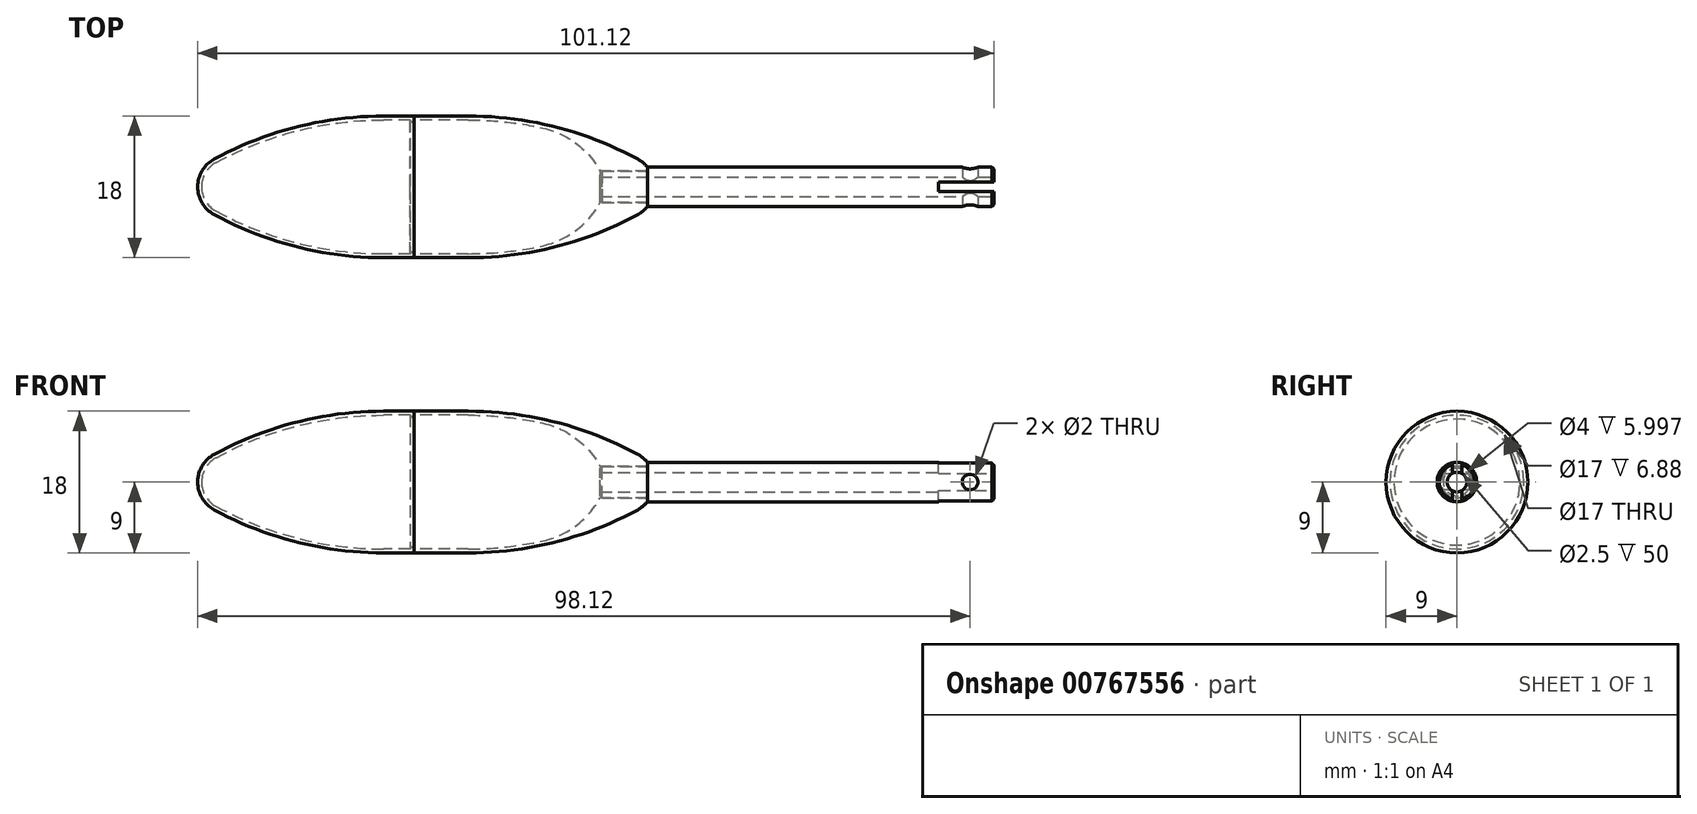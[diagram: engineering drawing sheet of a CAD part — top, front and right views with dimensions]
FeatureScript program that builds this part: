
annotation { "Feature Type Name" : "Feature", "Feature Type Description" : "" }
export const myFeature = defineFeature(function(context is Context, id is Id, definition is map)
    precondition{}
    {
        {
            var Q0;
            Q0=qCreatedBy(makeId("Front.planeOp"),FACE);
            var sketch = newSketch(context, id + "F0", { "sketchPlane" : qUnion([Q0])});
            skLineSegment(sketch, "E0", {"start": v(0, 0) * mm, "end": v(0, 8.5) * mm});
            skLineSegment(sketch, "E1", {"start": v(0, 8.5) * mm, "end": v(-3, 8.5) * mm});
            skLineSegment(sketch, "E2", {"start": v(-3, 8.5) * mm, "end": v(-3, 9) * mm});
            skLineSegment(sketch, "E3", {"start": v(-3, 9) * mm, "end": v(-6.88, 9) * mm});
            skArc(sketch, "E4", {"start": v(-6.88, 9) * mm, "mid": v(-18, 7.6) * mm, "end": v(-28.41, 3.51) * mm});
            skArc(sketch, "E5", {"start": v(-28.41, 3.51) * mm, "mid": v(-29.94, 2.04) * mm, "end": v(-30.5, 0) * mm});
            skLineSegment(sketch, "E6", {"start": v(-30.5, 0) * mm, "end": v(0, 0) * mm});
            skSolve(sketch);
        }
        {
            var Q0;
            Q0 = qSketchRegion(id + "F0", true);
            var Q1;
            Q1=sQuery(id+"F0.wireOp",EDGE,"E6");
            revolve(context, id + "F1", {"surfaceOperationType" : NewSurfaceOperationType.NEW, "entities" : qUnion([Q0]), "axis" : qUnion([Q1]), "revolveType" : RevolveType.FULL});
        }
        {
            var Q0;
            Q0=makeQuery(id+"F1.opRevolve","SWEPT_FACE",FACE,{"disambiguationData":[OSD([sQuery(id+"F0.wireOp",EDGE,"E0")])]});
            shell(context, id + "F2", {"entities" : qUnion([Q0]), "thickness" : 0.5 * mm});
        }
        {
            var Q0;
            Q0=makeQuery(id+"F2.opShell","OFFSET_EDGE",EDGE,{"disambiguationData":[OSD([sQuery(id+"F0.wireOp",EDGE,"E1"),sQuery(id+"F0.wireOp",EDGE,"E2")])]});
            chamfer(context, id + "F3", {"entities" : qUnion([Q0]), "width" : 0.5 * mm, "tangentPropagation" : true});
        }
        {
            var Q0;
            Q0=qCreatedBy(makeId("Front.planeOp"),FACE);
            var sketch = newSketch(context, id + "F4", { "sketchPlane" : qUnion([Q0])});
            skLineSegment(sketch, "E7", {"start": v(-3, 0) * mm, "end": v(-3, 9) * mm});
            skLineSegment(sketch, "E8", {"start": v(-3, 9) * mm, "end": v(3.88, 9) * mm});
            skArc(sketch, "E9", {"start": v(25.42, 3.51) * mm, "mid": v(15, 7.6) * mm, "end": v(3.88, 9) * mm});
            skArc(sketch, "E10", {"start": v(26.62, 2.5) * mm, "mid": v(26.07, 3.07) * mm, "end": v(25.42, 3.51) * mm});
            skLineSegment(sketch, "E11", {"start": v(26.62, 2.5) * mm, "end": v(26.62, 0) * mm});
            skLineSegment(sketch, "E12", {"start": v(26.62, 0) * mm, "end": v(-3, 0) * mm});
            skPoint(sketch, "E13.orphan", {"position": v(27.5, 0) * mm});
            skSolve(sketch);
        }
        {
            var Q0;
            Q0=qCreatedBy(makeId("Front.planeOp"),FACE);
            var sketch = newSketch(context, id + "F5", { "sketchPlane" : qUnion([Q0])});
            skLineSegment(sketch, "E14", {"start": v(-3, 0) * mm, "end": v(-3, 8.5) * mm});
            skLineSegment(sketch, "E15", {"start": v(-3, 8.5) * mm, "end": v(3.88, 8.5) * mm});
            skArc(sketch, "E16", {"start": v(13.29, 7.5) * mm, "mid": v(8.6, 8.25) * mm, "end": v(3.88, 8.5) * mm});
            skArc(sketch, "E17", {"start": v(20.62, 2) * mm, "mid": v(17.55, 5.55) * mm, "end": v(13.29, 7.5) * mm});
            skLineSegment(sketch, "E18", {"start": v(20.62, 2) * mm, "end": v(20.62, 0) * mm, "construction": true});
            skLineSegment(sketch, "E19", {"start": v(26.62, 0) * mm, "end": v(-3, 0) * mm});
            skLineSegment(sketch, "E20", {"start": v(20.62, 2) * mm, "end": v(26.62, 2) * mm});
            skLineSegment(sketch, "E21", {"start": v(26.62, 2) * mm, "end": v(26.62, 0) * mm});
            skSolve(sketch);
        }
        {
            var Q0;
            Q0 = qSketchRegion(id + "F4", true);
            var Q1;
            Q1=sQuery(id+"F4.wireOp",EDGE,"E12");
            revolve(context, id + "F6", {"surfaceOperationType" : NewSurfaceOperationType.NEW, "entities" : qUnion([Q0]), "axis" : qUnion([Q1]), "revolveType" : RevolveType.FULL});
        }
        {
            var Q0;
            Q0 = qSketchRegion(id + "F5", true);
            var Q1;
            Q1=sQuery(id+"F5.wireOp",EDGE,"E19");
            revolve(context, id + "F7", {"operationType" : NewBodyOperationType.REMOVE, "surfaceOperationType" : NewSurfaceOperationType.NEW, "entities" : qUnion([Q0]), "axis" : qUnion([Q1]), "revolveType" : RevolveType.FULL, "oppositeDirection" : true});
        }
        {
            var Q0;
            Q0=qCreatedBy(makeId("Front.planeOp"),FACE);
            var sketch = newSketch(context, id + "F8", { "sketchPlane" : qUnion([Q0])});
            skLineSegment(sketch, "E22", {"start": v(20.62, 1.25) * mm, "end": v(20.62, 2) * mm});
            skLineSegment(sketch, "E23", {"start": v(20.62, 2) * mm, "end": v(26.62, 2) * mm});
            skLineSegment(sketch, "E24", {"start": v(26.62, 2) * mm, "end": v(26.62, 2.5) * mm});
            skLineSegment(sketch, "E25", {"start": v(26.62, 2.5) * mm, "end": v(70.62, 2.5) * mm});
            skLineSegment(sketch, "E26", {"start": v(70.62, 2.5) * mm, "end": v(70.62, 1.25) * mm});
            skLineSegment(sketch, "E27", {"start": v(70.62, 0) * mm, "end": v(20.62, 0) * mm, "construction": true});
            skLineSegment(sketch, "E28", {"start": v(20.62, 1.25) * mm, "end": v(70.62, 1.25) * mm});
            skSolve(sketch);
        }
        {
            var Q0;
            Q0 = qSketchRegion(id + "F8", true);
            var Q1;
            Q1=sQuery(id+"F8.wireOp",EDGE,"E27");
            revolve(context, id + "F9", {"surfaceOperationType" : NewSurfaceOperationType.NEW, "entities" : qUnion([Q0]), "axis" : qUnion([Q1]), "revolveType" : RevolveType.FULL});
        }
        {
            var Q0;
            Q0=makeQuery(id+"F9.opRevolve","SWEPT_EDGE",EDGE,{"disambiguationData":[OSD([sQuery(id+"F8.wireOp",EDGE,"E22"),sQuery(id+"F8.wireOp",EDGE,"E23")])]});
            var Q1;
            Q1=makeQuery(id+"F9.opRevolve","SWEPT_EDGE",EDGE,{"disambiguationData":[OSD([sQuery(id+"F8.wireOp",EDGE,"E25"),sQuery(id+"F8.wireOp",EDGE,"E26")])]});
            chamfer(context, id + "F10", {"entities" : qUnion([Q0, Q1]), "width" : 0.25 * mm, "tangentPropagation" : true});
        }
        {
            var Q0;
            Q0=qCreatedBy(makeId("Front.planeOp"),FACE);
            var sketch = newSketch(context, id + "F11", { "sketchPlane" : qUnion([Q0])});
            skCircle(sketch, "E29", {"center": v(67.62, 0) * mm, "radius": 1 * mm});
            skSolve(sketch);
        }
        {
            var Q0;
            Q0 = qSketchRegion(id + "F11", true);
            extrude(context, id + "F12", {"entities" : qUnion([Q0]), "operationType" : NewBodyOperationType.REMOVE, "endBound" : BoundingType.SYMMETRIC, "oppositeDirection" : true, "depth" : 25 * mm, "offsetDistance" : 25 * mm});
        }
        {
            var Q0;
            Q0=makeQuery(id+"F9.opRevolve","SWEPT_FACE",FACE,{"disambiguationData":[OSD([sQuery(id+"F8.wireOp",EDGE,"E26")])]});
            var sketch = newSketch(context, id + "F13", { "sketchPlane" : qUnion([Q0])});
            skLineSegment(sketch, "E30.bottom", {"start": v(0.6, -3) * mm, "end": v(-0.6, -3) * mm});
            skLineSegment(sketch, "E30.top", {"start": v(0.6, 3) * mm, "end": v(-0.6, 3) * mm});
            skLineSegment(sketch, "E30.left", {"start": v(0.6, -3) * mm, "end": v(0.6, 3) * mm});
            skLineSegment(sketch, "E30.right", {"start": v(-0.6, -3) * mm, "end": v(-0.6, 3) * mm});
            skPoint(sketch, "E30.middle", {"position": v(0, 0) * mm});
            skSolve(sketch);
        }
        {
            var Q0;
            Q0 = qSketchRegion(id + "F13", true);
            extrude(context, id + "F14", {"entities" : qUnion([Q0]), "operationType" : NewBodyOperationType.REMOVE, "oppositeDirection" : true, "depth" : 7 * mm, "offsetDistance" : 25 * mm});
        }
    });
